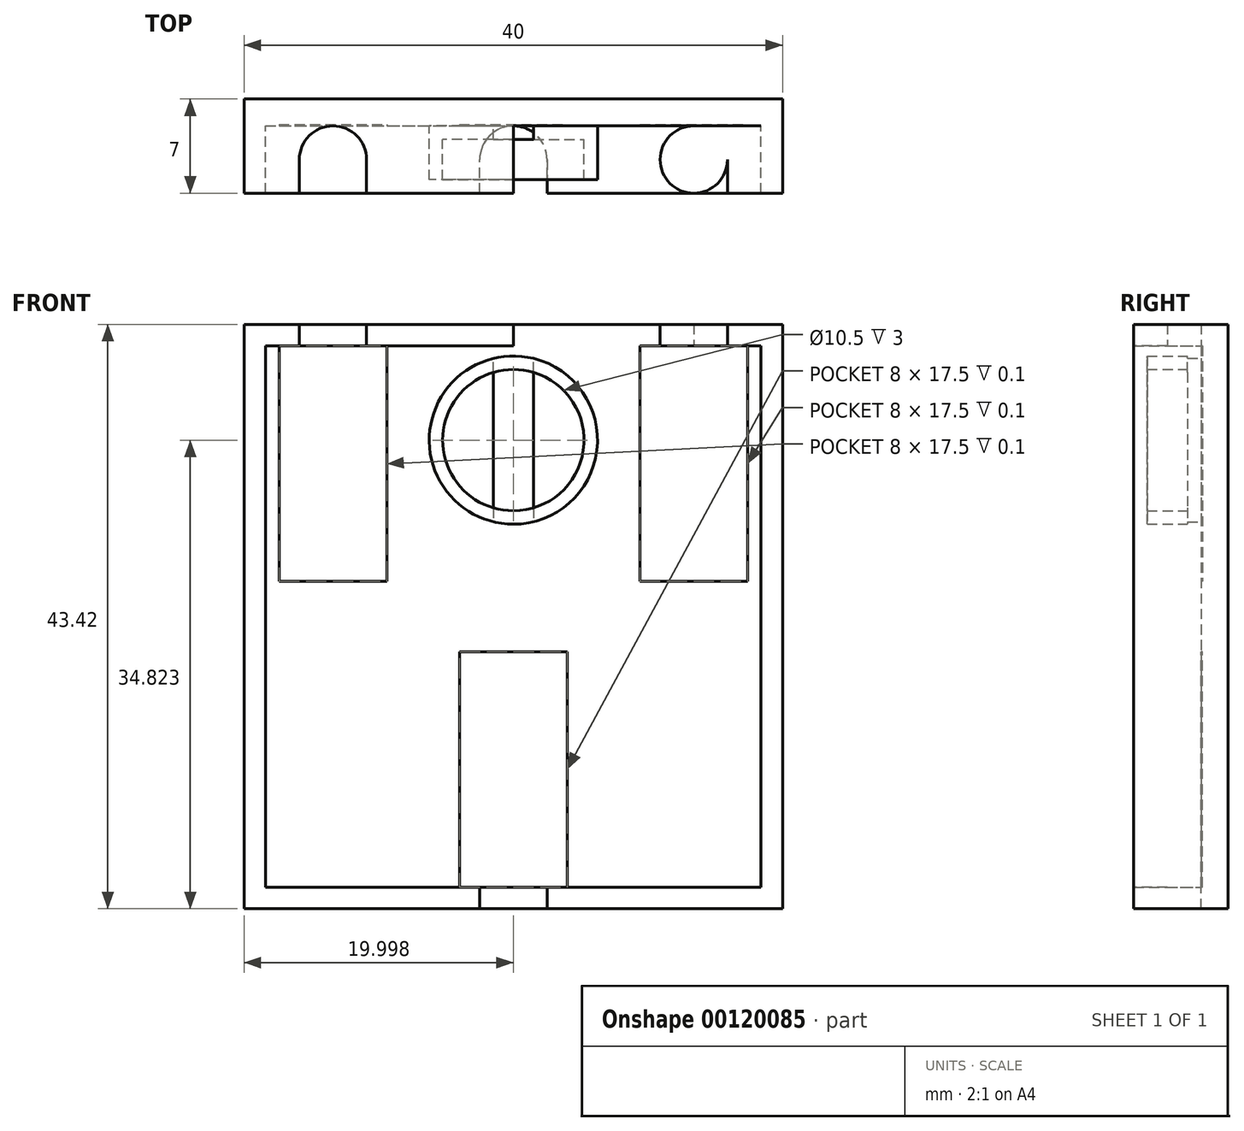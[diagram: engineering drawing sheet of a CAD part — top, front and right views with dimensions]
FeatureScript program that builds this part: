
annotation { "Feature Type Name" : "Feature", "Feature Type Description" : "" }
export const myFeature = defineFeature(function(context is Context, id is Id, definition is map)
    precondition{}
    {
        {
            var Q0;
            Q0=qCreatedBy(makeId("Front.planeOp"),FACE);
            var sketch = newSketch(context, id + "F0", { "sketchPlane" : qUnion([Q0])});
            skLineSegment(sketch, "E0.bottom", {"start": v(-35.75, 39) * mm, "end": v(4.25, 39) * mm});
            skLineSegment(sketch, "E0.top", {"start": v(-35.75, -4.42) * mm, "end": v(4.25, -4.42) * mm});
            skLineSegment(sketch, "E0.left", {"start": v(-35.75, 39) * mm, "end": v(-35.75, -4.42) * mm});
            skLineSegment(sketch, "E0.right", {"start": v(4.25, 39) * mm, "end": v(4.25, -4.42) * mm});
            skSolve(sketch);
        }
        {
            var Q0;
            Q0 = qSketchRegion(id + "F0", true);
            extrude(context, id + "F1", {"entities" : qUnion([Q0]), "depth" : 2 * mm});
        }
        {
            var Q0;
            Q0=makeQuery(id+"F1.opExtrude","CAP_FACE",FACE,{"disambiguationData":[OSD([sQuery(id+"F0.wireOp",EDGE,"E0.bottom"),sQuery(id+"F0.wireOp",EDGE,"E0.top"),sQuery(id+"F0.wireOp",EDGE,"E0.left"),sQuery(id+"F0.wireOp",EDGE,"E0.right")])],"isStart":false});
            var sketch = newSketch(context, id + "F2", { "sketchPlane" : qUnion([Q0])});
            skLineSegment(sketch, "E1.0", {"start": v(-35.75, 39) * mm, "end": v(4.25, 39) * mm});
            skLineSegment(sketch, "E1.1", {"start": v(-35.75, 39) * mm, "end": v(-35.75, -4.42) * mm});
            skLineSegment(sketch, "E1.3", {"start": v(-35.75, -4.42) * mm, "end": v(4.25, -4.42) * mm});
            skLineSegment(sketch, "E2.bottom", {"start": v(-34.15, 37.4) * mm, "end": v(2.65, 37.4) * mm});
            skLineSegment(sketch, "E2.top", {"start": v(-34.15, -2.82) * mm, "end": v(2.65, -2.82) * mm});
            skLineSegment(sketch, "E2.left", {"start": v(-34.15, 37.4) * mm, "end": v(-34.15, -2.82) * mm});
            skLineSegment(sketch, "E2.right", {"start": v(2.65, 37.4) * mm, "end": v(2.65, -2.82) * mm});
            skSolve(sketch);
        }
        {
            var Q0;
            Q0=makeQuery(id+"F2.imprint","IMPRINT",FACE,{"disambiguationData":[TD([[makeQuery(id+"F2.imprint","IMPRINT",EDGE,{"derivedFrom":sQuery(id+"F2.wireOp",EDGE,"E1.0")}),-1.0]])]});
            extrude(context, id + "F3", {"entities" : qUnion([Q0]), "operationType" : NewBodyOperationType.ADD, "depth" : 5 * mm});
        }
        {
            var Q0;
            Q0=makeQuery(id+"F3.opExtrude","SWEPT_FACE",FACE,{"disambiguationData":[OSD([sQuery(id+"F2.wireOp",EDGE,"E2.bottom")])]});
            var sketch = newSketch(context, id + "F4", { "sketchPlane" : qUnion([Q0])});
            skPoint(sketch, "E3", {"position": v(-29.15, 4.5) * mm});
            skCircle(sketch, "E4", {"center": v(-29.15, 4.5) * mm, "radius": 2.5 * mm});
            skLineSegment(sketch, "E5", {"start": v(-31.65, 4.5) * mm, "end": v(-31.65, 7) * mm});
            skLineSegment(sketch, "E6", {"start": v(-26.65, 4.5) * mm, "end": v(-26.65, 7) * mm});
            skLineSegment(sketch, "E7", {"start": v(-15.75, 7) * mm, "end": v(-15.75, 2) * mm});
            skCircle(sketch, "E8.MirrorC", {"center": v(-2.35, 4.5) * mm, "radius": 2.5 * mm});
            skLineSegment(sketch, "E9.MirrorCS", {"start": v(-4.85, 4.5) * mm, "end": v(-4.85, 7) * mm});
            skLineSegment(sketch, "E10.MirrorCS", {"start": v(0.15, 4.5) * mm, "end": v(0.15, 7) * mm});
            skSolve(sketch);
        }
        {
            var Q0;
            {var subQ0=sQuery(id+"F4.wireOp",EDGE,"E8.MirrorC");var subQ1=makeQuery(id+"F4.imprint","INTERSECT",VERTEX,{"derivedFrom":[subQ0,sQuery(id+"F4.wireOp",EDGE,"E9.MirrorCS")]});Q0=makeQuery(id+"F4.imprint","IMPRINT",FACE,{"disambiguationData":[TD([[makeQuery(id+"F4.imprint","IMPRINT",EDGE,{"disambiguationData":[TD([[subQ1,-1.0]])],"derivedFrom":subQ0}),-1.0]])]});}
            var Q1;
            {var subQ0=sQuery(id+"F4.wireOp",EDGE,"E4");var subQ1=makeQuery(id+"F4.imprint","INTERSECT",VERTEX,{"derivedFrom":[subQ0,sQuery(id+"F4.wireOp",EDGE,"E6")]});Q1=makeQuery(id+"F4.imprint","IMPRINT",FACE,{"disambiguationData":[TD([[makeQuery(id+"F4.imprint","IMPRINT",EDGE,{"disambiguationData":[TD([[subQ1,-1.0]])],"derivedFrom":subQ0}),1.0]])]});}
            var Q2;
            {var subQ0=sQuery(id+"F4.wireOp",EDGE,"E6");Q2=makeQuery(id+"F4.imprint","IMPRINT",FACE,{"disambiguationData":[TD([[makeQuery(id+"F4.imprint","IMPRINT",EDGE,{"derivedFrom":subQ0}),1.0]])]});}
            var Q3;
            {var subQ0=sQuery(id+"F4.wireOp",EDGE,"E5");Q3=makeQuery(id+"F4.imprint","IMPRINT",FACE,{"disambiguationData":[TD([[makeQuery(id+"F4.imprint","IMPRINT",EDGE,{"derivedFrom":subQ0}),-1.0]])]});}
            var Q4;
            {var subQ0=sQuery(id+"F4.wireOp",EDGE,"E9.MirrorCS");Q4=makeQuery(id+"F4.imprint","IMPRINT",FACE,{"disambiguationData":[TD([[makeQuery(id+"F4.imprint","IMPRINT",EDGE,{"derivedFrom":subQ0}),-1.0]])]});}
            var Q5;
            {var subQ0=sQuery(id+"F4.wireOp",EDGE,"E10.MirrorCS");Q5=makeQuery(id+"F4.imprint","IMPRINT",FACE,{"disambiguationData":[TD([[makeQuery(id+"F4.imprint","IMPRINT",EDGE,{"derivedFrom":subQ0}),1.0]])]});}
            extrude(context, id + "F5", {"entities" : qUnion([Q0, Q1, Q2, Q3, Q4, Q5]), "operationType" : NewBodyOperationType.REMOVE, "endBound" : BoundingType.UP_TO_NEXT, "oppositeDirection" : true, "depth" : 25 * mm});
        }
        {
            var Q0;
            Q0=makeQuery(id+"F1.opExtrude","CAP_FACE",FACE,{"disambiguationData":[OSD([sQuery(id+"F0.wireOp",EDGE,"E0.bottom"),sQuery(id+"F0.wireOp",EDGE,"E0.top"),sQuery(id+"F0.wireOp",EDGE,"E0.left"),sQuery(id+"F0.wireOp",EDGE,"E0.right")])],"isStart":false});
            var sketch = newSketch(context, id + "F6", { "sketchPlane" : qUnion([Q0])});
            skPoint(sketch, "E11", {"position": v(-15.75, 30.4) * mm});
            skPoint(sketch, "E11.positionSnap0", {"position": v(-15.75, 37.4) * mm});
            skCircle(sketch, "E12", {"center": v(-15.75, 30.4) * mm, "radius": 5.25 * mm});
            skLineSegment(sketch, "E13", {"start": v(-17.25, 35.43) * mm, "end": v(-17.25, 25.37) * mm});
            skLineSegment(sketch, "E14", {"start": v(-14.25, 35.43) * mm, "end": v(-14.25, 25.37) * mm});
            skCircle(sketch, "E15", {"center": v(-15.75, 30.4) * mm, "radius": 6.25 * mm});
            skLineSegment(sketch, "E16", {"start": v(-17.25, 35.43) * mm, "end": v(-17.25, 36.47) * mm});
            skLineSegment(sketch, "E17", {"start": v(-14.25, 35.43) * mm, "end": v(-14.25, 36.47) * mm});
            skLineSegment(sketch, "E18", {"start": v(-17.25, 25.37) * mm, "end": v(-17.25, 24.34) * mm});
            skLineSegment(sketch, "E19", {"start": v(-14.25, 25.37) * mm, "end": v(-14.25, 24.34) * mm});
            skSolve(sketch);
        }
        {
            var Q0;
            {var subQ0=sQuery(id+"F6.wireOp",EDGE,"E13");Q0=makeQuery(id+"F6.imprint","IMPRINT",FACE,{"disambiguationData":[TD([[makeQuery(id+"F6.imprint","IMPRINT",EDGE,{"derivedFrom":subQ0}),-1.0]])]});}
            var Q1;
            {var subQ0=sQuery(id+"F6.wireOp",EDGE,"E14");Q1=makeQuery(id+"F6.imprint","IMPRINT",FACE,{"disambiguationData":[TD([[makeQuery(id+"F6.imprint","IMPRINT",EDGE,{"derivedFrom":subQ0}),1.0]])]});}
            extrude(context, id + "F7", {"entities" : qUnion([Q0, Q1]), "operationType" : NewBodyOperationType.ADD, "depth" : 1 * mm});
        }
        {
            var Q0;
            Q0 = qSketchRegion(id + "F6", true);
            extrude(context, id + "F8", {"entities" : qUnion([Q0]), "operationType" : NewBodyOperationType.ADD, "depth" : 4 * mm});
        }
        {
            var Q0;
            {var subQ0=sQuery(id+"F6.wireOp",EDGE,"E16");Q0=makeQuery(id+"F6.imprint","IMPRINT",FACE,{"disambiguationData":[TD([[makeQuery(id+"F6.imprint","IMPRINT",EDGE,{"derivedFrom":subQ0}),-1.0]])]});}
            var Q1;
            {var subQ0=sQuery(id+"F6.wireOp",EDGE,"E18");Q1=makeQuery(id+"F6.imprint","IMPRINT",FACE,{"disambiguationData":[TD([[makeQuery(id+"F6.imprint","IMPRINT",EDGE,{"derivedFrom":subQ0}),1.0]])]});}
            extrude(context, id + "F9", {"entities" : qUnion([Q0, Q1]), "operationType" : NewBodyOperationType.REMOVE, "depth" : 1 * mm});
        }
        {
            var Q0;
            Q0=makeQuery(id+"F3.opExtrude","SWEPT_FACE",FACE,{"disambiguationData":[OSD([sQuery(id+"F2.wireOp",EDGE,"E2.top")])]});
            var sketch = newSketch(context, id + "F10", { "sketchPlane" : qUnion([Q0])});
            skPoint(sketch, "E20", {"position": v(-15.75, -7) * mm});
            skPoint(sketch, "E21", {"position": v(-15.75, -4.5) * mm});
            skCircle(sketch, "E22", {"center": v(-15.75, -4.5) * mm, "radius": 2.5 * mm});
            skLineSegment(sketch, "E23", {"start": v(-18.25, -4.5) * mm, "end": v(-18.25, -7) * mm});
            skLineSegment(sketch, "E24", {"start": v(-13.25, -4.5) * mm, "end": v(-13.25, -7) * mm});
            skSolve(sketch);
        }
        {
            var Q0;
            {var subQ0=sQuery(id+"F10.wireOp",EDGE,"E24");Q0=makeQuery(id+"F10.imprint","IMPRINT",FACE,{"disambiguationData":[TD([[makeQuery(id+"F10.imprint","IMPRINT",EDGE,{"derivedFrom":subQ0}),-1.0]])]});}
            var Q1;
            {var subQ0=sQuery(id+"F10.wireOp",EDGE,"E22");var subQ1=makeQuery(id+"F10.imprint","INTERSECT",VERTEX,{"derivedFrom":[subQ0,sQuery(id+"F10.wireOp",EDGE,"E24")]});Q1=makeQuery(id+"F10.imprint","IMPRINT",FACE,{"disambiguationData":[TD([[makeQuery(id+"F10.imprint","IMPRINT",EDGE,{"disambiguationData":[TD([[subQ1,-1.0]])],"derivedFrom":subQ0}),1.0]])]});}
            var Q2;
            {var subQ0=sQuery(id+"F10.wireOp",EDGE,"E23");Q2=makeQuery(id+"F10.imprint","IMPRINT",FACE,{"disambiguationData":[TD([[makeQuery(id+"F10.imprint","IMPRINT",EDGE,{"derivedFrom":subQ0}),1.0]])]});}
            extrude(context, id + "F11", {"entities" : qUnion([Q0, Q1, Q2]), "operationType" : NewBodyOperationType.REMOVE, "endBound" : BoundingType.UP_TO_NEXT, "oppositeDirection" : true, "depth" : 25 * mm});
        }
        {
            var Q0;
            {var subQ0=sQuery(id+"F6.wireOp",EDGE,"E15");var subQ1=sQuery(id+"F6.wireOp",EDGE,"E12");var subQ2=makeQuery(id+"F1.opExtrude","CAP_FACE",FACE,{"disambiguationData":[OSD([sQuery(id+"F0.wireOp",EDGE,"E0.bottom"),sQuery(id+"F0.wireOp",EDGE,"E0.top"),sQuery(id+"F0.wireOp",EDGE,"E0.left"),sQuery(id+"F0.wireOp",EDGE,"E0.right")])],"isStart":false});Q0=makeQuery(id+"F9.boolean.opBoolean","MERGE",FACE,{"derivedFrom":[makeQuery(id+"F8.boolean.opBoolean","SPLIT",FACE,{"disambiguationData":[TD([makeQuery(id+"F3.opExtrude","SWEPT_FACE",FACE,{"disambiguationData":[OSD([sQuery(id+"F2.wireOp",EDGE,"E2.bottom")])]})])],"derivedFrom":subQ2}),makeQuery(id+"F8.boolean.opBoolean","SPLIT",FACE,{"disambiguationData":[TD([makeQuery(id+"F7.opExtrude","SWEPT_FACE",FACE,{"disambiguationData":[OSD([sQuery(id+"F6.wireOp",EDGE,"E13")])]})])],"derivedFrom":subQ2}),makeQuery(id+"F9.opExtrude","CAP_FACE",FACE,{"disambiguationData":[OSD([subQ1,subQ0,sQuery(id+"F6.wireOp",EDGE,"E16"),sQuery(id+"F6.wireOp",EDGE,"E17")])],"isStart":true}),makeQuery(id+"F9.opExtrude","CAP_FACE",FACE,{"disambiguationData":[OSD([subQ1,subQ0,sQuery(id+"F6.wireOp",EDGE,"E18"),sQuery(id+"F6.wireOp",EDGE,"E19")])],"isStart":true})]});}
            var sketch = newSketch(context, id + "F12", { "sketchPlane" : qUnion([Q0])});
            skLineSegment(sketch, "E25.bottom", {"start": v(-33.15, 37.4) * mm, "end": v(-25.15, 37.4) * mm});
            skLineSegment(sketch, "E25.top", {"start": v(-33.15, 19.9) * mm, "end": v(-25.15, 19.9) * mm});
            skLineSegment(sketch, "E25.left", {"start": v(-33.15, 37.4) * mm, "end": v(-33.15, 19.9) * mm});
            skLineSegment(sketch, "E25.right", {"start": v(-25.15, 37.4) * mm, "end": v(-25.15, 19.9) * mm});
            skLineSegment(sketch, "E26", {"start": v(-15.75, 37.4) * mm, "end": v(-15.75, 12.57) * mm, "construction": true});
            skPoint(sketch, "E26.endSnap0", {"position": v(-15.75, 37.4) * mm});
            skLineSegment(sketch, "E27.MirrorCS", {"start": v(-6.35, 37.4) * mm, "end": v(-6.35, 19.9) * mm});
            skLineSegment(sketch, "E28.MirrorCS", {"start": v(1.65, 19.9) * mm, "end": v(-6.35, 19.9) * mm});
            skLineSegment(sketch, "E29.MirrorCS", {"start": v(1.65, 37.4) * mm, "end": v(1.65, 19.9) * mm});
            skLineSegment(sketch, "E30.MirrorCS", {"start": v(1.65, 37.4) * mm, "end": v(-6.35, 37.4) * mm});
            skLineSegment(sketch, "E31.bottom", {"start": v(-19.75, -2.82) * mm, "end": v(-11.75, -2.82) * mm});
            skLineSegment(sketch, "E31.top", {"start": v(-19.75, 14.68) * mm, "end": v(-11.75, 14.68) * mm});
            skLineSegment(sketch, "E31.left", {"start": v(-19.75, -2.82) * mm, "end": v(-19.75, 14.68) * mm});
            skLineSegment(sketch, "E31.right", {"start": v(-11.75, -2.82) * mm, "end": v(-11.75, 14.68) * mm});
            skSolve(sketch);
        }
        {
            var Q0;
            Q0=makeQuery(id+"F12.imprint","IMPRINT",FACE,{"disambiguationData":[TD([[makeQuery(id+"F12.imprint","IMPRINT",EDGE,{"derivedFrom":sQuery(id+"F12.wireOp",EDGE,"E25.top")}),1.0]])]});
            var Q1;
            {var subQ3=sQuery(id+"F12.wireOp",EDGE,"E27.MirrorCS");Q1=makeQuery(id+"F12.imprint","IMPRINT",FACE,{"disambiguationData":[TD([[makeQuery(id+"F12.imprint","IMPRINT",EDGE,{"derivedFrom":subQ3}),1.0]])]});}
            var Q2;
            Q2=makeQuery(id+"F12.imprint","IMPRINT",FACE,{"disambiguationData":[TD([[makeQuery(id+"F12.imprint","IMPRINT",EDGE,{"derivedFrom":sQuery(id+"F12.wireOp",EDGE,"E31.top")}),-1.0]])]});
            extrude(context, id + "F13", {"entities" : qUnion([Q0, Q1, Q2]), "operationType" : NewBodyOperationType.REMOVE, "oppositeDirection" : true, "depth" : 0.1 * mm});
        }
    });
